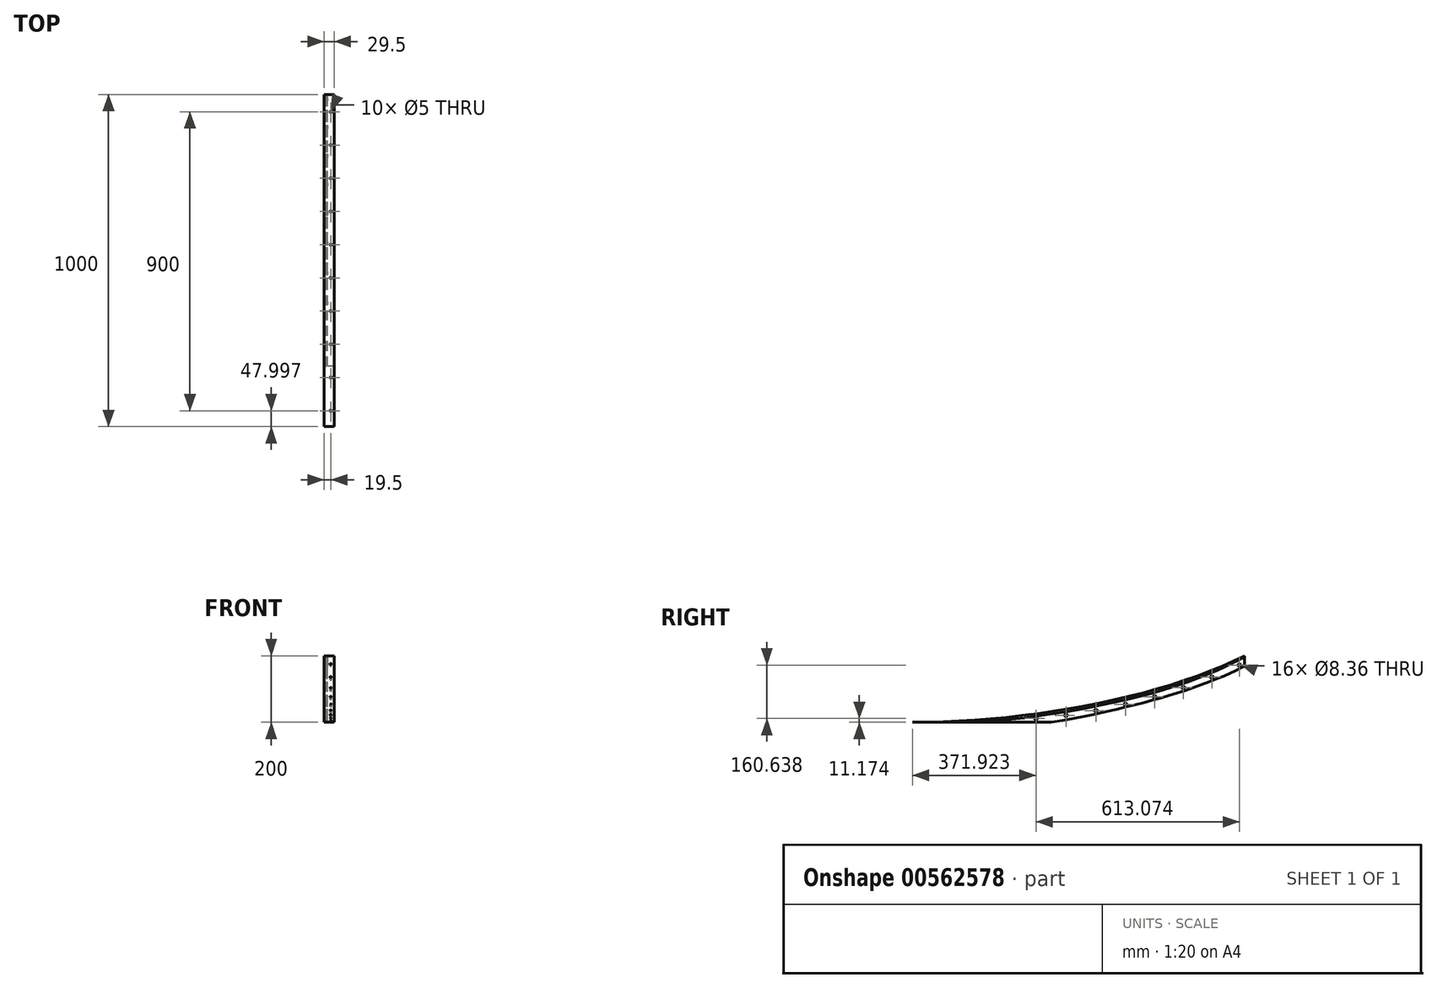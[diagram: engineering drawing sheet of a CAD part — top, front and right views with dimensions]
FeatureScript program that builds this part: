
annotation { "Feature Type Name" : "Feature", "Feature Type Description" : "" }
export const myFeature = defineFeature(function(context is Context, id is Id, definition is map)
    precondition{}
    {
        {
            var Q0;
            Q0=qCreatedBy(makeId("Right.planeOp"),FACE);
            var sketch = newSketch(context, id + "F0", { "sketchPlane" : qUnion([Q0])});
            skFitSpline(sketch, "E0", {"points": [v(-542.95, -39.95) * mm, v(457.05, 160.05) * mm], "startDerivative": vector(1064.65, 0) * mm, "endDerivative": vector(757.35, 377.28) * mm});
            skFitSpline(sketch, "E1.0", {"points": [v(-542.95, -42.95) * mm, v(-454.13, -42.95) * mm, v(-271.77, -33.66) * mm, v(-0.77, 6) * mm, v(251.07, 69.3) * mm, v(395.1, 125.84) * mm, v(458.38, 157.36) * mm]});
            skFitSpline(sketch, "E2.0", {"points": [v(-542.95, -67.95) * mm, v(-453.26, -67.95) * mm, v(-269.31, -58.57) * mm, v(-41.54, -25.24) * mm, v(131.25, 13.4) * mm, v(254.1, 48.12) * mm, v(368.23, 88.4) * mm, v(437.17, 118.87) * mm, v(469.53, 134.99) * mm]});
            skLineSegment(sketch, "E3", {"start": v(457.05, 160.05) * mm, "end": v(457.05, 100.76) * mm});
            skLineSegment(sketch, "E4", {"start": v(-542.95, -39.95) * mm, "end": v(-47.7, -39.95) * mm});
            skSolve(sketch);
        }
        {
            var Q0;
            {var subQ0=sQuery(id+"F0.wireOp",EDGE,"E0");Q0=makeQuery(id+"F0.imprint","IMPRINT",FACE,{"disambiguationData":[TD([[makeQuery(id+"F0.imprint","IMPRINT",EDGE,{"derivedFrom":subQ0}),-1.0]])]});}
            extrude(context, id + "F1", {"entities" : qUnion([Q0]), "depth" : 25 * mm, "offsetDistance" : 25 * mm, "hasSecondDirection" : true, "secondDirectionOppositeDirection" : true, "secondDirectionDepth" : 4.5 * mm});
        }
        {
            var Q0;
            {var subQ0=sQuery(id+"F0.wireOp",EDGE,"E3");var subQ1=sQuery(id+"F0.wireOp",EDGE,"E1.0");var subQ2=makeQuery(id+"F0.imprint","INTERSECT",VERTEX,{"derivedFrom":[subQ1,subQ0]});Q0=makeQuery(id+"F0.imprint","IMPRINT",FACE,{"disambiguationData":[TD([[makeQuery(id+"F0.imprint","IMPRINT",EDGE,{"disambiguationData":[TD([[subQ2,1.0]])],"derivedFrom":subQ1}),-1.0]])]});}
            extrude(context, id + "F2", {"entities" : qUnion([Q0]), "operationType" : NewBodyOperationType.ADD, "endBound" : BoundingType.SYMMETRIC, "depth" : 9 * mm, "offsetDistance" : 25 * mm});
        }
        {
            var Q0;
            {var subQ0=sQuery(id+"F0.wireOp",EDGE,"E3");var subQ1=sQuery(id+"F0.wireOp",EDGE,"E1.0");var subQ2=makeQuery(id+"F0.imprint","INTERSECT",VERTEX,{"derivedFrom":[subQ1,subQ0]});Q0=makeQuery(id+"F0.imprint","IMPRINT",FACE,{"disambiguationData":[TD([[makeQuery(id+"F0.imprint","IMPRINT",EDGE,{"disambiguationData":[TD([[subQ2,1.0]])],"derivedFrom":subQ1}),-1.0]])]});}
            extrude(context, id + "F3", {"entities" : qUnion([Q0]), "operationType" : NewBodyOperationType.REMOVE, "endBound" : BoundingType.SYMMETRIC, "oppositeDirection" : true, "depth" : 3 * mm, "offsetDistance" : 25 * mm});
        }
        {
            var Q0;
            Q0=qCreatedBy(makeId("Top.planeOp"),FACE);
            var sketch = newSketch(context, id + "F4", { "sketchPlane" : qUnion([Q0])});
            skCircle(sketch, "E5", {"center": v(15, -494.95) * mm, "radius": 2.5 * mm});
            skCircle(sketch, "E6.0.1.0", {"center": v(15, -394.95) * mm, "radius": 2.5 * mm});
            skCircle(sketch, "E6.0.2.0", {"center": v(15, -294.95) * mm, "radius": 2.5 * mm});
            skCircle(sketch, "E6.0.3.0", {"center": v(15, -194.95) * mm, "radius": 2.5 * mm});
            skCircle(sketch, "E6.0.4.0", {"center": v(15, -94.95) * mm, "radius": 2.5 * mm});
            skCircle(sketch, "E6.0.5.0", {"center": v(15, 5.05) * mm, "radius": 2.5 * mm});
            skCircle(sketch, "E6.0.6.0", {"center": v(15, 105.05) * mm, "radius": 2.5 * mm});
            skCircle(sketch, "E6.0.7.0", {"center": v(15, 205.05) * mm, "radius": 2.5 * mm});
            skCircle(sketch, "E6.0.8.0", {"center": v(15, 305.05) * mm, "radius": 2.5 * mm});
            skCircle(sketch, "E6.0.9.0", {"center": v(15, 405.05) * mm, "radius": 2.5 * mm});
            skCircle(sketch, "E6.1.0.0", {"center": v(-15, -494.95) * mm, "radius": 2.5 * mm});
            skCircle(sketch, "E6.1.1.0", {"center": v(-15, -394.95) * mm, "radius": 2.5 * mm});
            skCircle(sketch, "E6.1.2.0", {"center": v(-15, -294.95) * mm, "radius": 2.5 * mm});
            skCircle(sketch, "E6.1.3.0", {"center": v(-15, -194.95) * mm, "radius": 2.5 * mm});
            skCircle(sketch, "E6.1.4.0", {"center": v(-15, -94.95) * mm, "radius": 2.5 * mm});
            skCircle(sketch, "E6.1.5.0", {"center": v(-15, 5.05) * mm, "radius": 2.5 * mm});
            skCircle(sketch, "E6.1.6.0", {"center": v(-15, 105.05) * mm, "radius": 2.5 * mm});
            skCircle(sketch, "E6.1.7.0", {"center": v(-15, 205.05) * mm, "radius": 2.5 * mm});
            skCircle(sketch, "E6.1.8.0", {"center": v(-15, 305.05) * mm, "radius": 2.5 * mm});
            skCircle(sketch, "E6.1.9.0", {"center": v(-15, 405.05) * mm, "radius": 2.5 * mm});
            skLineSegment(sketch, "E6.direction1", {"start": v(15, -494.95) * mm, "end": v(-15, -494.95) * mm, "construction": true});
            skLineSegment(sketch, "E6.direction2", {"start": v(15, -494.95) * mm, "end": v(15, -394.95) * mm, "construction": true});
            skSolve(sketch);
        }
        {
            var Q0;
            Q0=qSketchRegion(id+"F4",true);
            extrude(context, id + "F5", {"entities" : qUnion([Q0]), "operationType" : NewBodyOperationType.REMOVE, "endBound" : BoundingType.SYMMETRIC, "oppositeDirection" : true, "depth" : 300 * mm, "offsetDistance" : 25 * mm});
        }
        {
            var Q0;
            Q0=qCreatedBy(makeId("Right.planeOp"),FACE);
            var sketch = newSketch(context, id + "F6", { "sketchPlane" : qUnion([Q0])});
            skCircle(sketch, "E7", {"center": v(442.05, 131.86) * mm, "radius": 4.18 * mm});
            skCircle(sketch, "E8.1.0", {"center": v(358.45, 95.94) * mm, "radius": 4.18 * mm});
            skCircle(sketch, "E8.2.0", {"center": v(273.16, 64.23) * mm, "radius": 4.18 * mm});
            skCircle(sketch, "E8.3.0", {"center": v(186.4, 36.8) * mm, "radius": 4.18 * mm});
            skCircle(sketch, "E8.4.0", {"center": v(98.38, 13.74) * mm, "radius": 4.18 * mm});
            skCircle(sketch, "E8.5.0", {"center": v(9.32, -4.9) * mm, "radius": 4.18 * mm});
            skCircle(sketch, "E8.6.0", {"center": v(-80.55, -19.09) * mm, "radius": 4.18 * mm});
            skCircle(sketch, "E8.7.0", {"center": v(-171.03, -28.78) * mm, "radius": 4.18 * mm});
            skPoint(sketch, "E8.center", {"position": v(-320, 1790) * mm});
            skLineSegment(sketch, "E8.anchor1", {"start": v(-320, 1790) * mm, "end": v(442.05, 131.86) * mm, "construction": true});
            skLineSegment(sketch, "E8.anchor2", {"start": v(-320, 1790) * mm, "end": v(-171.03, -28.78) * mm, "construction": true});
            skSolve(sketch);
        }
        {
            var Q0;
            Q0=qSketchRegion(id+"F6",true);
            extrude(context, id + "F7", {"entities" : qUnion([Q0]), "operationType" : NewBodyOperationType.REMOVE, "endBound" : BoundingType.SYMMETRIC, "oppositeDirection" : true, "depth" : 25 * mm, "offsetDistance" : 25 * mm});
        }
    });
